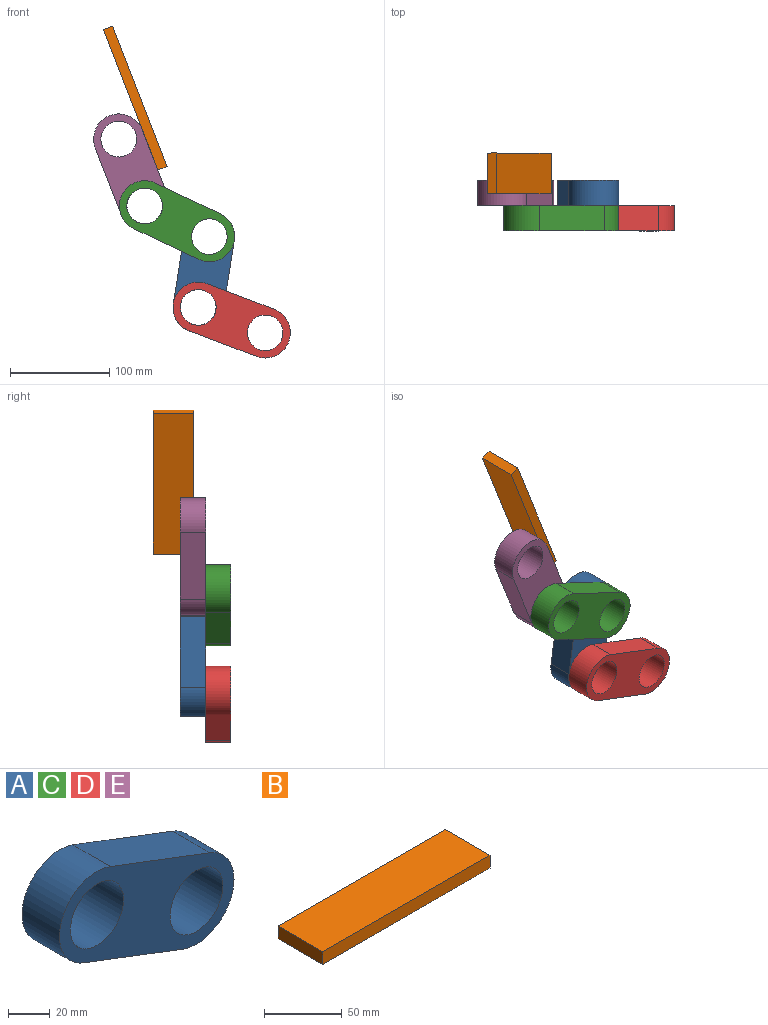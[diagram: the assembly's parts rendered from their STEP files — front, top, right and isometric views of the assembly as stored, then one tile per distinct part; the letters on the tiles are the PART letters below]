
ASSEMBLY  parts=5 mates=4
PART A: 8 faces, bbox 118.3x25.4x76.4 mm
  f0: plane 67.45x25.64mm, normal (0.36,0,0.93), area 1832.9mm2, adj f1,f4,f6,f7
  f1: cylinder r=25.4mm len=49.14mm, axis (0,1,0), area 2026.8mm2, adj f0,f2,f6,f7
  f2: plane 67.45x25.64mm, normal (-0.36,0,-0.93), area 1832.9mm2, adj f1,f4,f6,f7
  f3: cylinder r=17.92mm len=35.83mm, axis (0,1,0), area 2859.2mm2, adj f6,f7
  f4: cylinder r=25.4mm len=49.14mm, axis (0,1,0), area 2026.8mm2, adj f0,f2,f6,f7
  f5: cylinder r=18.01mm len=36.02mm, axis (0,1,0), area 2874.6mm2, adj f6,f7
  f6: plane 118.25x76.44mm, normal (0,-1,0), area 3665mm2, adj f0,f1,f2,f3,f4,f5
  f7: plane 118.25x76.44mm, normal (0,1,0), area 3665mm2, adj f0,f1,f2,f3,f4,f5
PART B: 6 faces, bbox 151.8x40.6x10 mm
  f0: plane 40.64x10.04mm, normal (1,0,0), area 407.9mm2, adj f1,f3,f4,f5
  f1: plane 151.76x40.64mm, normal (0,0,1), area 6167.7mm2, adj f0,f2,f4,f5
  f2: plane 40.64x10.04mm, normal (-1,0,0), area 407.9mm2, adj f1,f3,f4,f5
  f3: plane 151.76x40.64mm, normal (0,0,-1), area 6167.7mm2, adj f0,f2,f4,f5
  f4: plane 151.76x10.04mm, normal (0,-1,0), area 1523.2mm2, adj f0,f1,f2,f3
  f5: plane 151.76x10.04mm, normal (0,1,0), area 1523.2mm2, adj f0,f1,f2,f3
PART C: same geometry as A
PART D: same geometry as A
PART E: same geometry as A
PLACE A rot(axis=(0,1,0),78.1deg) t=(-70.52,31.37,34.59)mm
PLACE B rot(axis=(0,1,0),68.8deg) t=(-204.24,58.58,312.03)mm fixed
PLACE C rot(axis=(0,1,0),4.6deg) t=(-59.29,5.97,105.87)mm
PLACE D t=(-3.07,5.97,8.95)mm fixed
PLACE E rot(axis=(0,1,0),48deg) t=(-124.49,31.37,136.78)mm
MATE revolute D.f1 <-> A.f3  axis (0,1,0) through (-70.52,5.97,34.59)mm
MATE revolute C.f3 <-> A.f1  axis (0,1,0) through (-59.29,5.97,105.87)mm
MATE revolute C.f1 <-> E.f3  axis (0,1,0) through (-124.49,5.97,136.78)mm
MATE planar B.f3 <-> E.f0  axis (-0.93,0,-0.36) through (-138.71,38.26,243.67)mm
